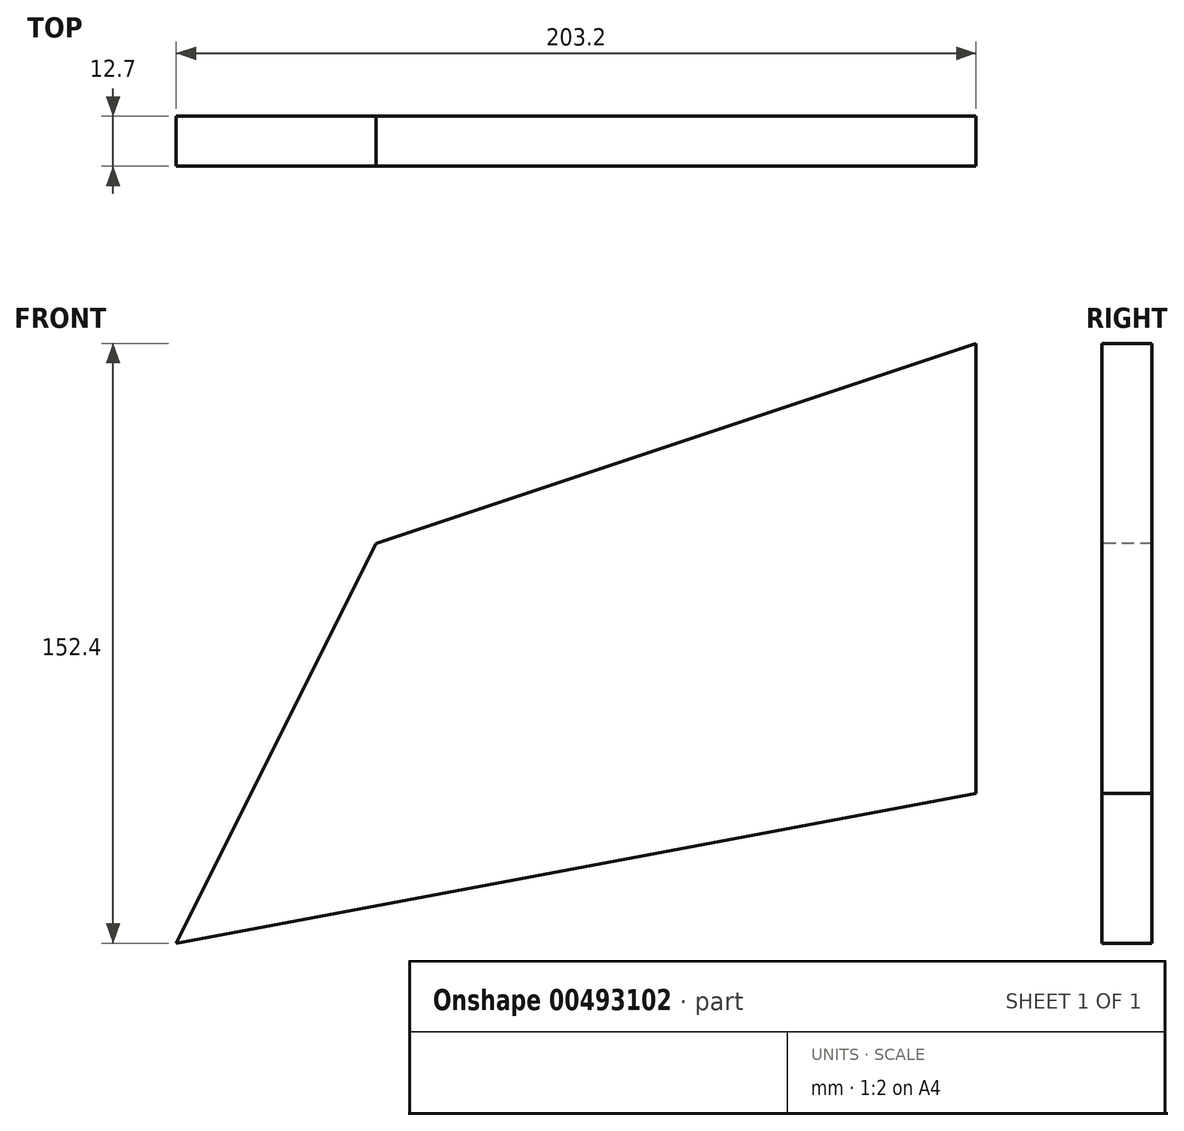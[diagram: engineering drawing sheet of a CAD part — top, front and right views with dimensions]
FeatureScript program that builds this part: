
annotation { "Feature Type Name" : "Feature", "Feature Type Description" : "" }
export const myFeature = defineFeature(function(context is Context, id is Id, definition is map)
    precondition{}
    {
        {
            var Q0;
            Q0=qCreatedBy(makeId("Front.planeOp"),FACE);
            var sketch = newSketch(context, id + "F0", { "sketchPlane" : qUnion([Q0])});
            skLineSegment(sketch, "E0.right", {"start": v(101.6, 101.6) * mm, "end": v(101.6, -12.7) * mm});
            skLineSegment(sketch, "E1", {"start": v(-101.6, -50.8) * mm, "end": v(-50.8, 50.8) * mm});
            skLineSegment(sketch, "E2", {"start": v(-50.8, 50.8) * mm, "end": v(101.6, 101.6) * mm});
            skLineSegment(sketch, "E3", {"start": v(-101.6, -50.8) * mm, "end": v(101.6, -12.7) * mm});
            skPoint(sketch, "E4.end.orphan", {"position": v(101.6, -50.8) * mm});
            skPoint(sketch, "E0.left.start.orphan", {"position": v(-101.6, 50.8) * mm});
            skSolve(sketch);
        }
        {
            var Q0;
            Q0=makeQuery(id+"F0.imprint","IMPRINT",FACE,{"disambiguationData":[TD([[makeQuery(id+"F0.imprint","IMPRINT",EDGE,{"derivedFrom":sQuery(id+"F0.wireOp",EDGE,"E0.right")}),-1.0]])]});
            extrude(context, id + "F1", {"entities" : qUnion([Q0]), "oppositeDirection" : true, "depth" : 12.7 * mm});
        }
    });
